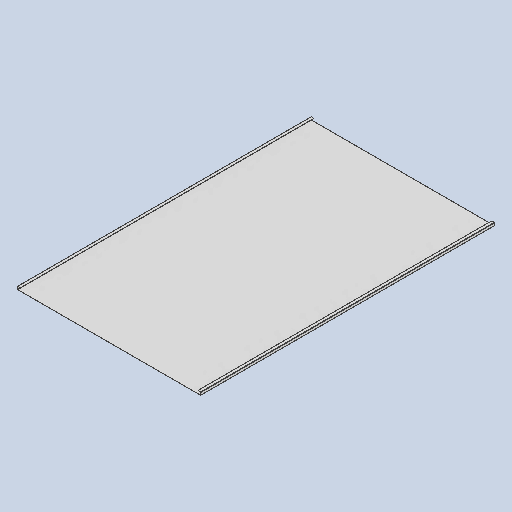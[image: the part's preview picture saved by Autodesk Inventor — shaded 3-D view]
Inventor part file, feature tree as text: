
AUTODESK INVENTOR PART (.ipt)
format: ipt  version: 2025 (Build 290162010, 162A)  size: 195,072 bytes
history: native  units: mm
features: sheet_metal_op x13, other x6, sketch x5, chamfer x1
ambient origin geometry x8: Origin, YZ Plane, XZ Plane, XY Plane, X Axis, Y Axis, Z Axis, Center Point
bodies: Body1 (feature_tree)
feature tree (25):
  sheet_metal_op  "Face1"
  sheet_metal_op  "Flange2"
  sheet_metal_op  "Flange3"
  sheet_metal_op  "Flange4"
  sheet_metal_op  "Flange5"
  chamfer  "Corner Round1"
  sketch  "Sketch6"  dims[d12=23.212879mm]
  other  "Plate2"
  sketch  "Sketch11"  dims[d52=612.6mm]
  other  "Plate4"
  sheet_metal_op  "Bend3"
  sheet_metal_op  "Corner3"
  sketch  "Sketch12"  dims[d53=980.0mm]
  other  "Plate5"
  sheet_metal_op  "Bend4"
  sheet_metal_op  "Corner4"
  sketch  "Sketch13"  dims[d54=0.5mm]
  other  "Plate6"
  sheet_metal_op  "Bend5"
  sheet_metal_op  "Corner5"
  sketch  "Sketch14"  dims[d84=0.5mm d85=0.25mm d86=1.0mm d87=0.5mm d88=10.0mm d89=90.0deg d90=0.5mm d91=2.0mm d92=0.5mm d93=0.5mm d94=0.5mm d95=0.25mm d96=1.0mm d97=0.5mm d98=10.0mm d99=90.0deg d100=0.5mm d101=2.0mm d102=0.5mm d103=0.5mm d104=0.5mm d105=0.25mm d106=1.0mm d107=0.5mm d108=10.0mm d109=90.0deg d110=0.5mm d111=2.0mm d112=0.5mm d113=0.5mm d114=0.5mm d115=0.25mm d116=1.0mm d117=0.5mm d118=10.0mm d119=90.0deg d120=0.5mm d121=2.0mm d122=0.5mm d123=0.5mm d124=4.0mm]
  other  "Plate7"
  sheet_metal_op  "Bend6"
  sheet_metal_op  "Corner6"
  other  "Definition1"
